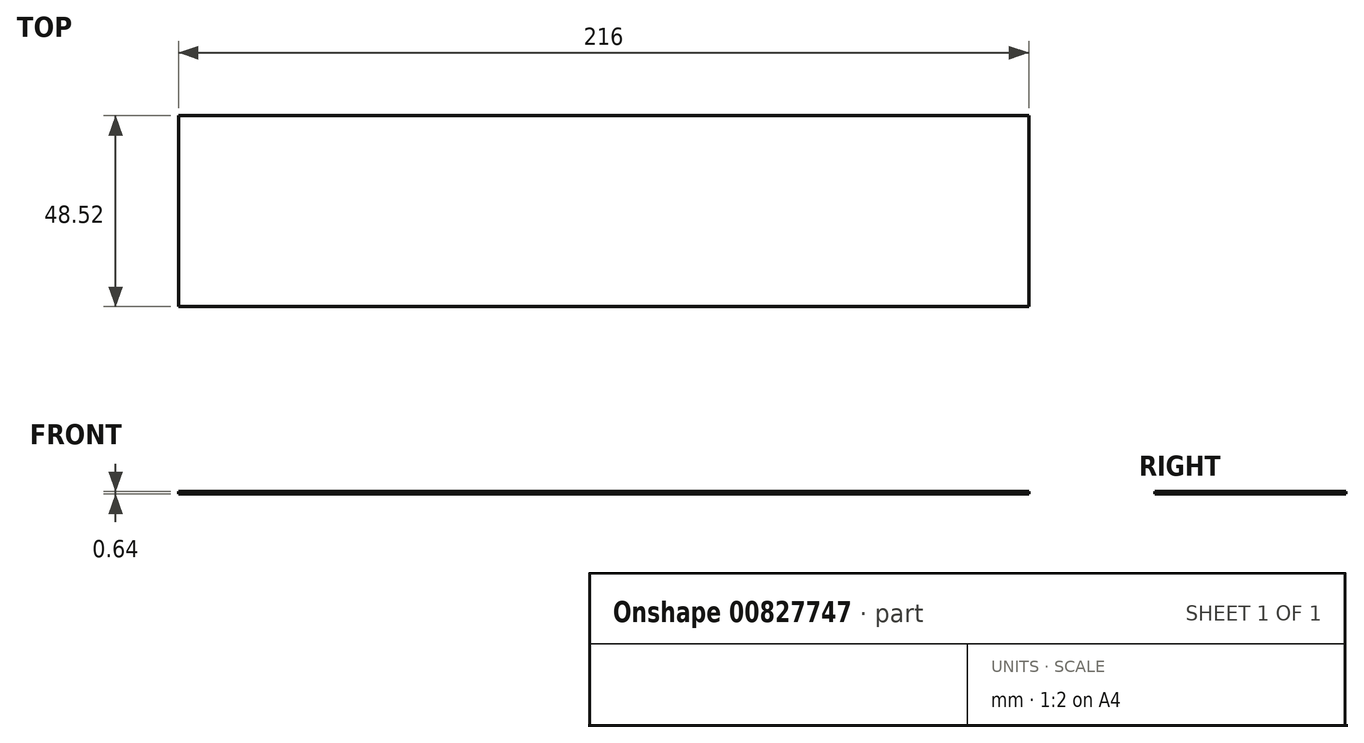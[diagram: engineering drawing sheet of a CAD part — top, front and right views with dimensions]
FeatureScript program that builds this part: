
annotation { "Feature Type Name" : "Feature", "Feature Type Description" : "" }
export const myFeature = defineFeature(function(context is Context, id is Id, definition is map)
    precondition{}
    {
        {
            var Q0;
            Q0=qCreatedBy(makeId("Top.planeOp"),FACE);
            var sketch = newSketch(context, id + "F0", { "sketchPlane" : qUnion([Q0])});
            skLineSegment(sketch, "E0.bottom", {"start": v(-186.89, 30.47) * mm, "end": v(29.11, 30.47) * mm});
            skLineSegment(sketch, "E0.top", {"start": v(-186.89, -18.05) * mm, "end": v(29.11, -18.05) * mm});
            skLineSegment(sketch, "E0.left", {"start": v(-186.89, 30.47) * mm, "end": v(-186.89, -18.05) * mm});
            skLineSegment(sketch, "E0.right", {"start": v(29.11, 30.47) * mm, "end": v(29.11, -18.05) * mm});
            skLineSegment(sketch, "E1.0", {"start": v(-131.09, 29.03) * mm, "end": v(-127.4, 29.03) * mm});
            skPoint(sketch, "E2.0", {"position": v(-53.88, -16.62) * mm});
            skPoint(sketch, "E3.0", {"position": v(-102.95, -16.62) * mm});
            skLineSegment(sketch, "E4.0", {"start": v(-170.15, -10.69) * mm, "end": v(-170.15, 6.94) * mm});
            skPoint(sketch, "E5.0", {"position": v(12.37, 2.94) * mm});
            skSolve(sketch);
        }
        {
            var Q0;
            Q0=makeQuery(id+"F0.imprint","IMPRINT",FACE,{"disambiguationData":[TD([[makeQuery(id+"F0.imprint","IMPRINT",EDGE,{"derivedFrom":sQuery(id+"F0.wireOp",EDGE,"E0.bottom")}),-1.0]])]});
            extrude(context, id + "F1", {"entities" : qUnion([Q0]), "depth" : 0.64 * mm, "offsetDistance" : 25.4 * mm});
        }
    });
